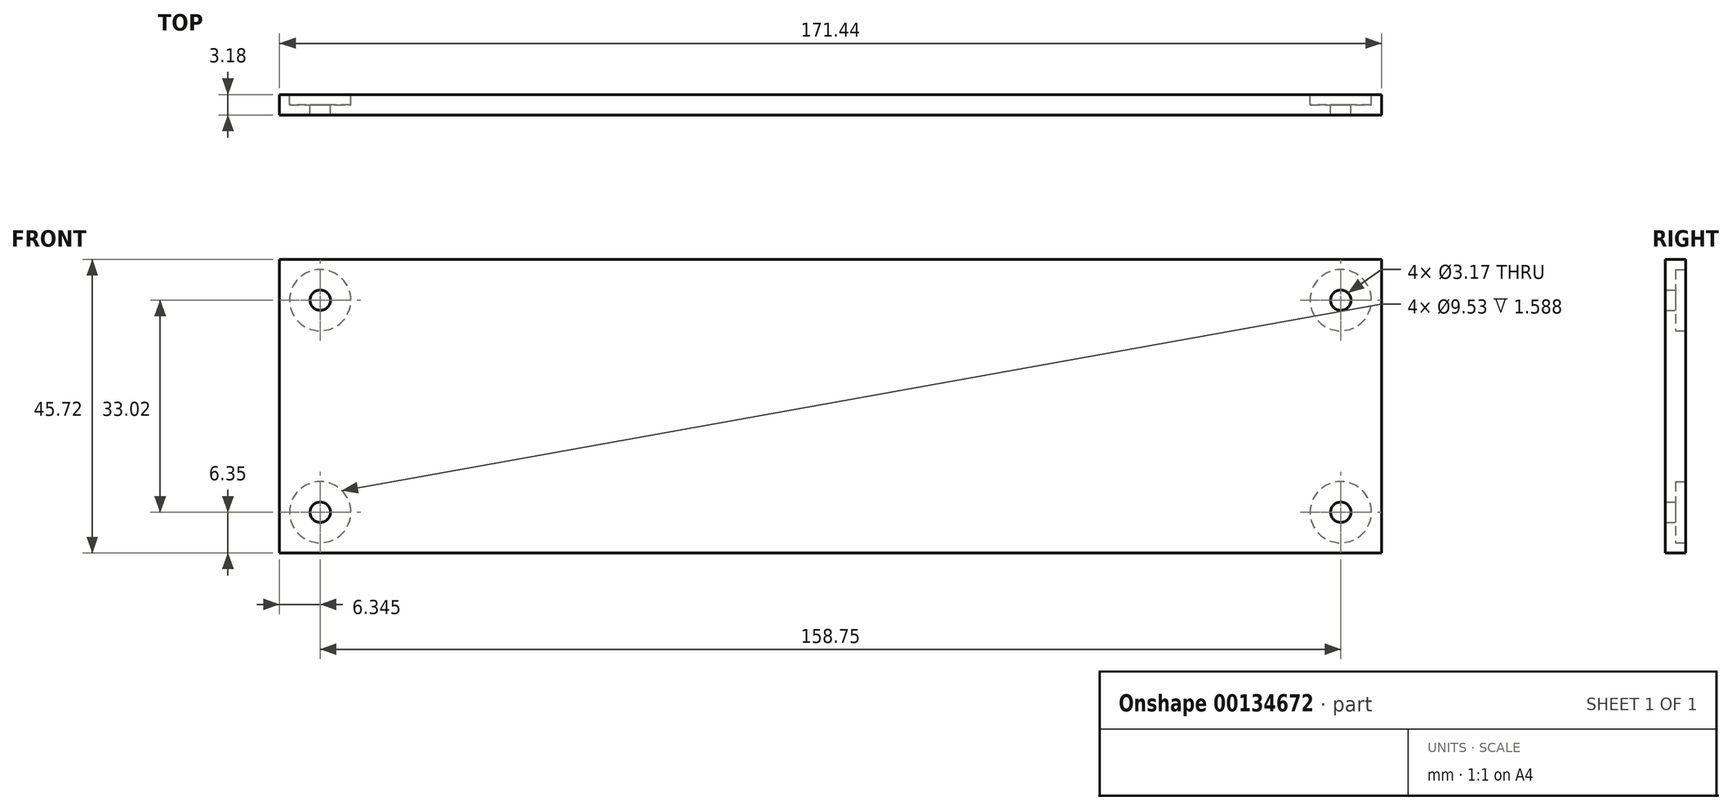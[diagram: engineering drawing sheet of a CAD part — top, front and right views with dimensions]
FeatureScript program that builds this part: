
annotation { "Feature Type Name" : "Feature", "Feature Type Description" : "" }
export const myFeature = defineFeature(function(context is Context, id is Id, definition is map)
    precondition{}
    {
        {
            var Q0;
            Q0=qCreatedBy(makeId("Front.planeOp"),FACE);
            var sketch = newSketch(context, id + "F0", { "sketchPlane" : qUnion([Q0])});
            skLineSegment(sketch, "E0.bottom", {"start": v(85.73, -22.86) * mm, "end": v(-85.73, -22.86) * mm});
            skLineSegment(sketch, "E0.top", {"start": v(85.73, 22.86) * mm, "end": v(-85.73, 22.86) * mm});
            skLineSegment(sketch, "E0.left", {"start": v(85.73, -22.86) * mm, "end": v(85.73, 22.86) * mm});
            skLineSegment(sketch, "E0.right", {"start": v(-85.73, -22.86) * mm, "end": v(-85.73, 22.86) * mm});
            skPoint(sketch, "E0.middle", {"position": v(0, 0) * mm});
            skSolve(sketch);
        }
        {
            var Q0;
            Q0 = qSketchRegion(id + "F0", true);
            extrude(context, id + "F1", {"entities" : qUnion([Q0]), "depth" : 3.17 * mm});
        }
        {
            var Q0;
            Q0=qCreatedBy(makeId("Front.planeOp"),FACE);
            var sketch = newSketch(context, id + "F2", { "sketchPlane" : qUnion([Q0])});
            skLineSegment(sketch, "E1.bottom", {"start": v(79.38, -16.51) * mm, "end": v(-79.37, -16.51) * mm});
            skLineSegment(sketch, "E1.top", {"start": v(79.37, 16.51) * mm, "end": v(-79.38, 16.5) * mm});
            skLineSegment(sketch, "E1.left", {"start": v(79.38, -16.5) * mm, "end": v(79.37, 16.51) * mm});
            skLineSegment(sketch, "E1.right", {"start": v(-79.37, -16.51) * mm, "end": v(-79.38, 16.5) * mm});
            skPoint(sketch, "E1.middle", {"position": v(0, 0) * mm});
            skSolve(sketch);
        }
        {
            var Q0;
            Q0=sQuery(id+"F2.wireOp",VERTEX,"E1.top.end");
            var Q1;
            Q1=sQuery(id+"F2.wireOp",VERTEX,"E1.left.end");
            var Q2;
            Q2=sQuery(id+"F2.wireOp",VERTEX,"E1.left.start");
            var Q3;
            Q3=sQuery(id+"F2.wireOp",VERTEX,"E1.right.start");
            var Q4;
            Q4=makeQuery(id+"F1.opExtrude","SWEPT_BODY",BODY,{"disambiguationData":[OSD([sQuery(id+"F0.wireOp",EDGE,"E0.bottom"),sQuery(id+"F0.wireOp",EDGE,"E0.top"),sQuery(id+"F0.wireOp",EDGE,"E0.left"),sQuery(id+"F0.wireOp",EDGE,"E0.right")])]});
            hole(context, id + "F3", {"style" : HoleStyle.C_BORE, "endStyle" : HoleEndStyle.THROUGH, "oppositeDirection" : true, "holeDiameter" : 3.17 * mm, "cBoreDiameter" : 9.52 * mm, "cBoreDepth" : 1.59 * mm, "locations" : qUnion([Q0, Q1, Q2, Q3]), "scope" : qUnion([Q4]), "isTappedThrough" : true});
        }
    });
